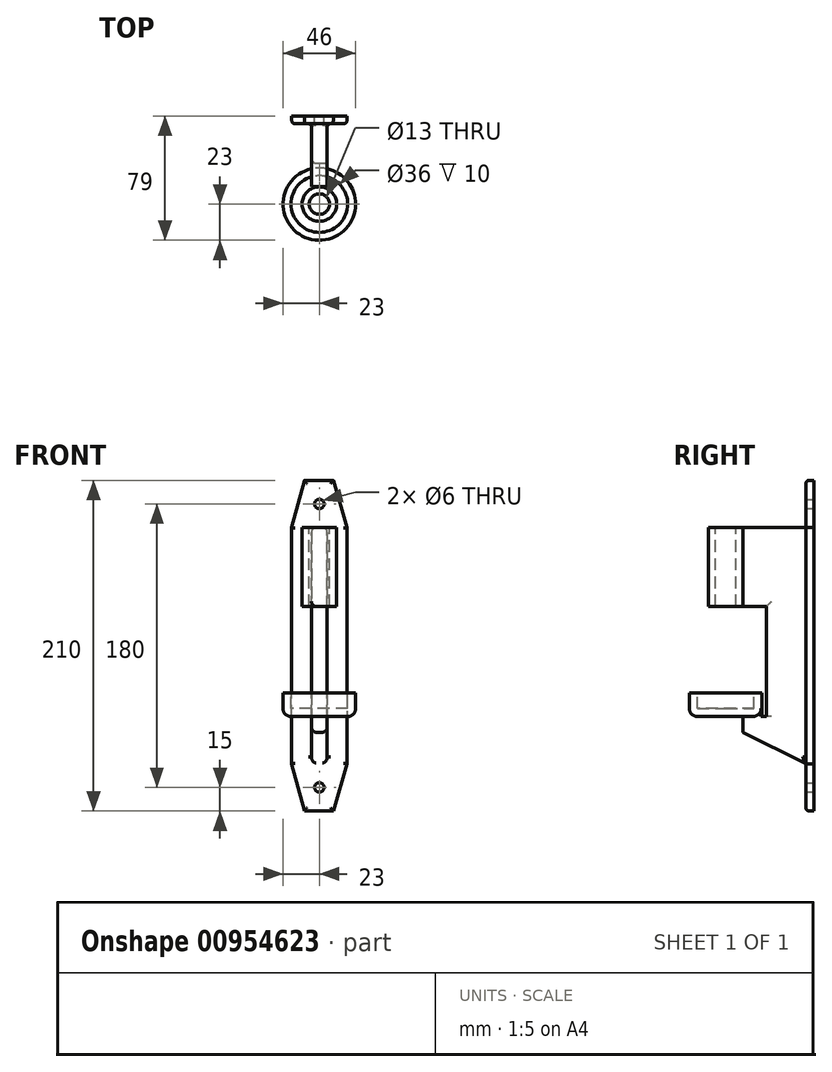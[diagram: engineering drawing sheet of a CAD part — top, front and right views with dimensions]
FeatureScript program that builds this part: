
annotation { "Feature Type Name" : "Feature", "Feature Type Description" : "" }
export const myFeature = defineFeature(function(context is Context, id is Id, definition is map)
    precondition{}
    {
        {
            var Q0;
            Q0=qCreatedBy(makeId("Front.planeOp"),FACE);
            var sketch = newSketch(context, id + "F0", { "sketchPlane" : qUnion([Q0])});
            skLineSegment(sketch, "E0.bottom", {"start": v(17.5, -105) * mm, "end": v(-17.5, -105) * mm, "construction": true});
            skLineSegment(sketch, "E0.top", {"start": v(17.5, 105) * mm, "end": v(-17.5, 105) * mm, "construction": true});
            skLineSegment(sketch, "E0.left", {"start": v(17.5, -105) * mm, "end": v(17.5, 105) * mm, "construction": true});
            skLineSegment(sketch, "E0.right", {"start": v(-17.5, -105) * mm, "end": v(-17.5, 105) * mm, "construction": true});
            skPoint(sketch, "E0.middle", {"position": v(0, 0) * mm});
            skLineSegment(sketch, "E1", {"start": v(-9.5, 105) * mm, "end": v(-9.5, -105) * mm, "construction": true});
            skLineSegment(sketch, "E2", {"start": v(-17.5, 75) * mm, "end": v(17.5, 75) * mm, "construction": true});
            skLineSegment(sketch, "E3", {"start": v(8.88, 105) * mm, "end": v(8.88, -105) * mm, "construction": true});
            skLineSegment(sketch, "E4", {"start": v(17.5, -75) * mm, "end": v(-17.5, -75) * mm, "construction": true});
            skLineSegment(sketch, "E5", {"start": v(-9.5, 105) * mm, "end": v(-17.5, 75) * mm});
            skLineSegment(sketch, "E6", {"start": v(-17.5, -75) * mm, "end": v(-9.5, -105) * mm});
            skLineSegment(sketch, "E7", {"start": v(8.88, -105) * mm, "end": v(17.5, -75) * mm});
            skLineSegment(sketch, "E8", {"start": v(17.5, 75) * mm, "end": v(8.88, 105) * mm});
            skLineSegment(sketch, "E9", {"start": v(-9.5, 105) * mm, "end": v(8.88, 105) * mm});
            skLineSegment(sketch, "E10", {"start": v(17.5, 75) * mm, "end": v(17.5, -75) * mm});
            skLineSegment(sketch, "E11", {"start": v(8.88, -105) * mm, "end": v(-9.5, -105) * mm});
            skLineSegment(sketch, "E12", {"start": v(-17.5, -75) * mm, "end": v(-17.5, 75) * mm});
            skSolve(sketch);
        }
        {
            var Q0;
            Q0 = qSketchRegion(id + "F0", true);
            extrude(context, id + "F1", {"entities" : qUnion([Q0]), "depth" : 5 * mm, "offsetDistance" : 25 * mm});
        }
        {
            var Q0;
            Q0=qCreatedBy(makeId("Right.planeOp"),FACE);
            var sketch = newSketch(context, id + "F2", { "sketchPlane" : qUnion([Q0])});
            skLineSegment(sketch, "E13", {"start": v(-5, 75) * mm, "end": v(-45, 75) * mm});
            skLineSegment(sketch, "E14", {"start": v(-45, 75) * mm, "end": v(-45, -55) * mm});
            skLineSegment(sketch, "E15", {"start": v(-45, -55) * mm, "end": v(-5, -75) * mm});
            skLineSegment(sketch, "E16", {"start": v(-5, -75) * mm, "end": v(-5, 75) * mm});
            skPoint(sketch, "E17", {"position": v(-5, 0) * mm});
            skSolve(sketch);
        }
        {
            var Q0;
            Q0 = qSketchRegion(id + "F2", true);
            extrude(context, id + "F3", {"entities" : qUnion([Q0]), "operationType" : NewBodyOperationType.ADD, "depth" : 5 * mm, "offsetDistance" : 25 * mm, "hasSecondDirection" : true, "secondDirectionOppositeDirection" : true, "secondDirectionDepth" : 5 * mm});
        }
        {
            var Q0;
            Q0=makeQuery(id+"F3.opExtrude","CAP_FACE",FACE,{"disambiguationData":[OSD([sQuery(id+"F2.wireOp",EDGE,"E13"),sQuery(id+"F2.wireOp",EDGE,"E14"),sQuery(id+"F2.wireOp",EDGE,"E15"),sQuery(id+"F2.wireOp",EDGE,"E16")])],"isStart":false});
            var sketch = newSketch(context, id + "F4", { "sketchPlane" : qUnion([Q0])});
            skLineSegment(sketch, "E18", {"start": v(-45, 25) * mm, "end": v(-30, 25) * mm});
            skLineSegment(sketch, "E19", {"start": v(-30, 25) * mm, "end": v(-30, -45) * mm});
            skLineSegment(sketch, "E20", {"start": v(-30, -45) * mm, "end": v(-45, -45) * mm});
            skLineSegment(sketch, "E21", {"start": v(-45, -45) * mm, "end": v(-45, 25) * mm});
            skSolve(sketch);
        }
        {
            var Q0;
            Q0 = qSketchRegion(id + "F4", true);
            extrude(context, id + "F5", {"entities" : qUnion([Q0]), "operationType" : NewBodyOperationType.REMOVE, "oppositeDirection" : true, "depth" : 25 * mm, "offsetDistance" : 25 * mm});
        }
        {
            var Q0;
            Q0=makeQuery(id+"F3.opExtrude","SWEPT_FACE",FACE,{"disambiguationData":[OSD([sQuery(id+"F2.wireOp",EDGE,"E13")])]});
            var sketch = newSketch(context, id + "F6", { "sketchPlane" : qUnion([Q0])});
            skCircle(sketch, "E22", {"center": v(0, -56) * mm, "radius": 11 * mm});
            skCircle(sketch, "E23", {"center": v(0, -56) * mm, "radius": 6.5 * mm});
            skSolve(sketch);
        }
        {
            var Q0;
            Q0 = qSketchRegion(id + "F6", true);
            var Q1;
            Q1=makeQuery(id+"F5.boolean.opBoolean","COPY",FACE,{"derivedFrom":makeQuery(id+"F5.opExtrude","SWEPT_FACE",FACE,{"disambiguationData":[OSD([sQuery(id+"F4.wireOp",EDGE,"E18")])]})});
            extrude(context, id + "F7", {"entities" : qUnion([Q0]), "operationType" : NewBodyOperationType.ADD, "endBound" : BoundingType.UP_TO_SURFACE, "oppositeDirection" : true, "depth" : 25 * mm, "endBoundEntityFace" : qUnion([Q1]), "offsetDistance" : 25 * mm});
        }
        {
            var Q0;
            Q0=makeQuery(id+"F5.boolean.opBoolean","COPY",FACE,{"derivedFrom":makeQuery(id+"F5.opExtrude","SWEPT_FACE",FACE,{"disambiguationData":[OSD([sQuery(id+"F4.wireOp",EDGE,"E20")])]})});
            var sketch = newSketch(context, id + "F8", { "sketchPlane" : qUnion([Q0])});
            skCircle(sketch, "E24", {"center": v(0, -56) * mm, "radius": 23 * mm});
            skSolve(sketch);
        }
        {
            var Q0;
            Q0 = qSketchRegion(id + "F8", true);
            extrude(context, id + "F9", {"entities" : qUnion([Q0]), "operationType" : NewBodyOperationType.ADD, "depth" : 15 * mm, "offsetDistance" : 25 * mm});
        }
        {
            var Q0;
            Q0=makeQuery(id+"F9.opExtrude","CAP_FACE",FACE,{"disambiguationData":[OSD([sQuery(id+"F8.wireOp",EDGE,"E24")])],"isStart":false});
            var sketch = newSketch(context, id + "F10", { "sketchPlane" : qUnion([Q0])});
            skCircle(sketch, "E25.0", {"center": v(0, -56) * mm, "radius": 18 * mm});
            skSolve(sketch);
        }
        {
            var Q0;
            Q0 = qSketchRegion(id + "F10", true);
            extrude(context, id + "F11", {"entities" : qUnion([Q0]), "operationType" : NewBodyOperationType.REMOVE, "oppositeDirection" : true, "depth" : 10 * mm, "offsetDistance" : 25 * mm});
        }
        {
            var Q0;
            {var subQ0=sQuery(id+"F8.wireOp",EDGE,"E24");Q0=makeQuery(id+"F9.boolean.opBoolean","SPLIT",EDGE,{"disambiguationData":[topologyDisambiguationEdgeConnected([makeQuery(id+"F9.opExtrude","CAP_FACE",FACE,{"disambiguationData":[OSD([subQ0])],"isStart":true})])],"derivedFrom":makeQuery(id+"F9.opExtrude","CAP_EDGE",EDGE,{"disambiguationData":[OSD([subQ0])],"isStart":true})});}
            fillet(context, id + "F12", {"entities" : qUnion([Q0]), "radius" : 5 * mm, "tangentPropagation" : true, "allowEdgeOverflow" : false});
        }
        {
            var Q0;
            Q0=makeQuery(id+"F3.opExtrude","CAP_EDGE",EDGE,{"disambiguationData":[OSD([sQuery(id+"F2.wireOp",EDGE,"E15")])],"isStart":true});
            var Q1;
            Q1=makeQuery(id+"F3.opExtrude","CAP_EDGE",EDGE,{"disambiguationData":[OSD([sQuery(id+"F2.wireOp",EDGE,"E15")])],"isStart":false});
            var Q2;
            Q2=makeQuery(id+"F3.opExtrude","CAP_EDGE",EDGE,{"disambiguationData":[OSD([sQuery(id+"F2.wireOp",EDGE,"E13")])],"isStart":true});
            var Q3;
            Q3=makeQuery(id+"F3.opExtrude","CAP_EDGE",EDGE,{"disambiguationData":[OSD([sQuery(id+"F2.wireOp",EDGE,"E13")])],"isStart":false});
            var Q4;
            Q4=makeQuery(id+"F5.boolean.opBoolean","INTERSECT",EDGE,{"derivedFrom":[makeQuery(id+"F3.opExtrude","CAP_FACE",FACE,{"disambiguationData":[OSD([sQuery(id+"F2.wireOp",EDGE,"E13"),sQuery(id+"F2.wireOp",EDGE,"E14"),sQuery(id+"F2.wireOp",EDGE,"E15"),sQuery(id+"F2.wireOp",EDGE,"E16")])],"isStart":true}),makeQuery(id+"F5.opExtrude","SWEPT_FACE",FACE,{"disambiguationData":[OSD([sQuery(id+"F4.wireOp",EDGE,"E19")])]})]});
            var Q5;
            Q5=makeQuery(id+"F5.boolean.opBoolean","COPY",EDGE,{"derivedFrom":makeQuery(id+"F5.opExtrude","CAP_EDGE",EDGE,{"disambiguationData":[OSD([sQuery(id+"F4.wireOp",EDGE,"E19")])],"isStart":true})});
            var Q6;
            Q6=makeQuery(id+"F5.boolean.opBoolean","COPY",EDGE,{"derivedFrom":makeQuery(id+"F5.opExtrude","CAP_EDGE",EDGE,{"disambiguationData":[OSD([sQuery(id+"F4.wireOp",EDGE,"E18")])],"isStart":true})});
            var Q7;
            Q7=makeQuery(id+"F5.boolean.opBoolean","INTERSECT",EDGE,{"derivedFrom":[makeQuery(id+"F3.opExtrude","CAP_FACE",FACE,{"disambiguationData":[OSD([sQuery(id+"F2.wireOp",EDGE,"E13"),sQuery(id+"F2.wireOp",EDGE,"E14"),sQuery(id+"F2.wireOp",EDGE,"E15"),sQuery(id+"F2.wireOp",EDGE,"E16")])],"isStart":true}),makeQuery(id+"F5.opExtrude","SWEPT_FACE",FACE,{"disambiguationData":[OSD([sQuery(id+"F4.wireOp",EDGE,"E18")])]})]});
            fillet(context, id + "F13", {"entities" : qUnion([Q0, Q1, Q2, Q3, Q4, Q5, Q6, Q7]), "radius" : 3 * mm, "tangentPropagation" : true, "allowEdgeOverflow" : false});
        }
        {
            var Q0;
            Q0=makeQuery(id+"F1.opExtrude","CAP_FACE",FACE,{"disambiguationData":[OSD([sQuery(id+"F0.wireOp",EDGE,"E5"),sQuery(id+"F0.wireOp",EDGE,"E6"),sQuery(id+"F0.wireOp",EDGE,"E7"),sQuery(id+"F0.wireOp",EDGE,"E8"),sQuery(id+"F0.wireOp",EDGE,"E9"),sQuery(id+"F0.wireOp",EDGE,"E10"),sQuery(id+"F0.wireOp",EDGE,"E11"),sQuery(id+"F0.wireOp",EDGE,"E12")])],"isStart":false});
            fillet(context, id + "F14", {"entities" : qUnion([Q0]), "radius" : 2 * mm, "tangentPropagation" : true, "allowEdgeOverflow" : false});
        }
        {
            var Q0;
            Q0=makeQuery(id+"F1.opExtrude","CAP_FACE",FACE,{"disambiguationData":[OSD([sQuery(id+"F0.wireOp",EDGE,"E5"),sQuery(id+"F0.wireOp",EDGE,"E6"),sQuery(id+"F0.wireOp",EDGE,"E7"),sQuery(id+"F0.wireOp",EDGE,"E8"),sQuery(id+"F0.wireOp",EDGE,"E9"),sQuery(id+"F0.wireOp",EDGE,"E10"),sQuery(id+"F0.wireOp",EDGE,"E11"),sQuery(id+"F0.wireOp",EDGE,"E12")])],"isStart":true});
            var sketch = newSketch(context, id + "F15", { "sketchPlane" : qUnion([Q0])});
            skCircle(sketch, "E26", {"center": v(0, 90) * mm, "radius": 3 * mm});
            skCircle(sketch, "E27", {"center": v(0, -90) * mm, "radius": 3 * mm});
            skSolve(sketch);
        }
        {
            var Q0;
            Q0 = qSketchRegion(id + "F15", true);
            extrude(context, id + "F16", {"entities" : qUnion([Q0]), "operationType" : NewBodyOperationType.REMOVE, "endBound" : BoundingType.UP_TO_NEXT, "oppositeDirection" : true, "depth" : 25 * mm, "offsetDistance" : 25 * mm});
        }
    });
